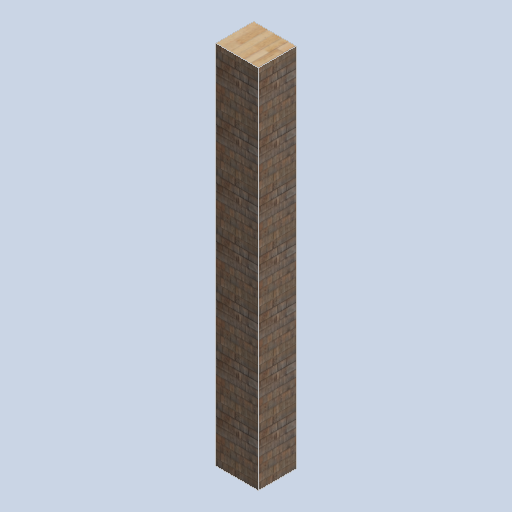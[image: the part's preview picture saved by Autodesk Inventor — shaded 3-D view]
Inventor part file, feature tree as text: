
AUTODESK INVENTOR PART (.ipt)
format: ipt  version: 2024.2 (Build 282272000, 272)  size: 164,864 bytes
history: native  units: in
note: dims shown in document units (in); Inventor stores cm internally (conversion verified against a paired STEP export)
features: other x3, sketch x1
ambient origin geometry x8: Origin, YZ Plane, XZ Plane, XY Plane, X Axis, Y Axis, Z Axis, Center Point
bodies: Solid1 (feature_tree)
feature tree (4):
  other  "support_column_01.ipt"
  other  "Solid1::support_column_01.ipt"
  other  "TaggingFeature1"
  sketch  "Sketch1"  dims[d0=0.3937in]
